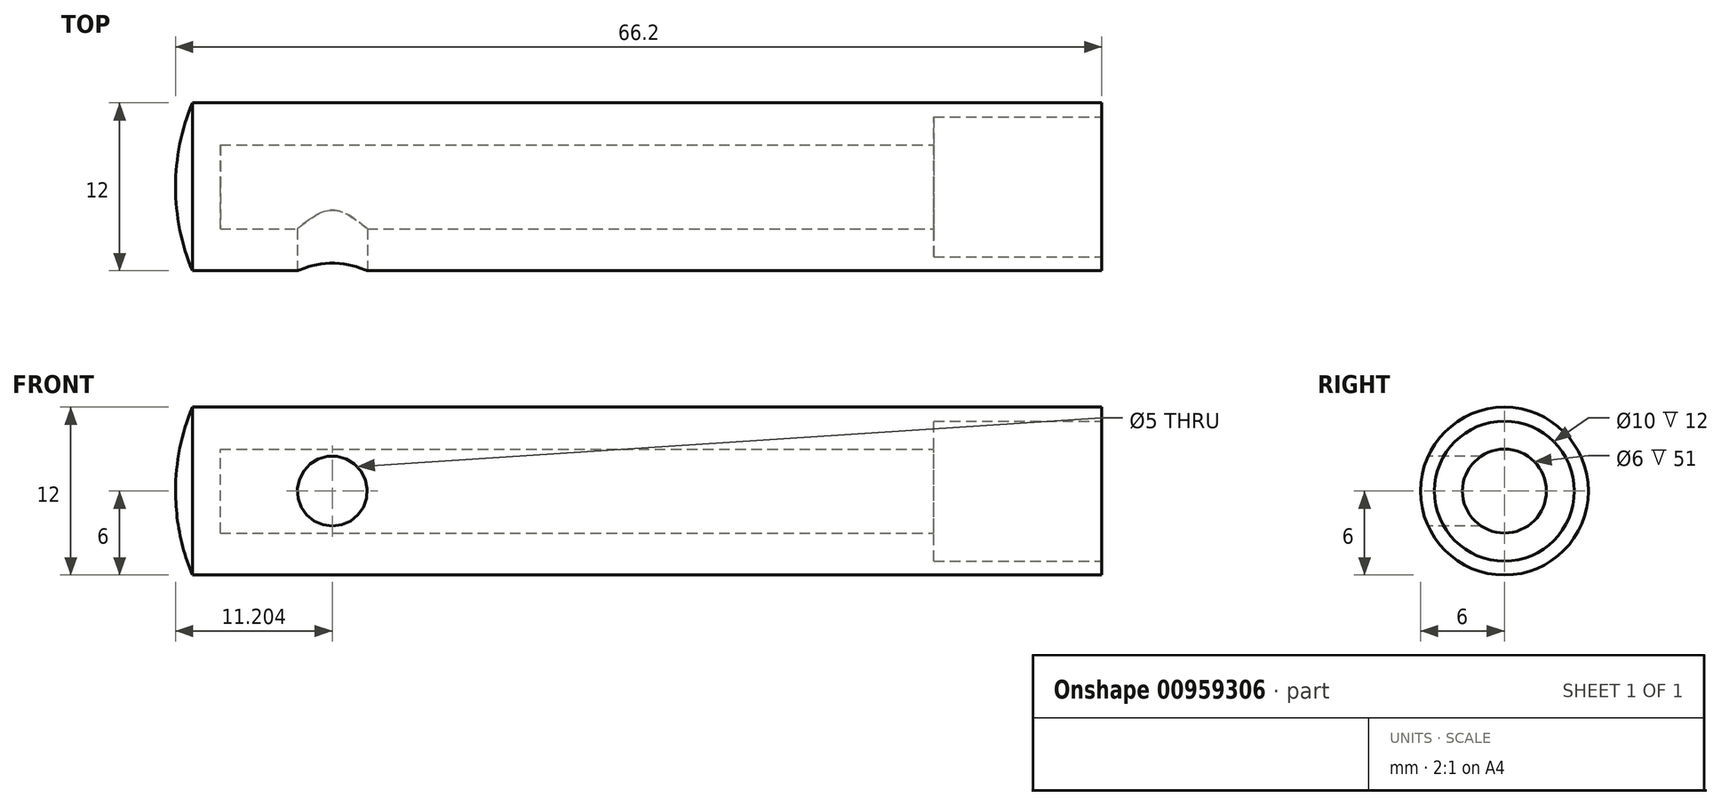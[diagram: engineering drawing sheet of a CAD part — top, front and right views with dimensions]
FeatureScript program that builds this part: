
annotation { "Feature Type Name" : "Feature", "Feature Type Description" : "" }
export const myFeature = defineFeature(function(context is Context, id is Id, definition is map)
    precondition{}
    {
        {
            var Q0;
            Q0=qCreatedBy(makeId("Front.planeOp"),FACE);
            var sketch = newSketch(context, id + "F0", { "sketchPlane" : qUnion([Q0])});
            skLineSegment(sketch, "E0", {"start": v(-36.24, -6) * mm, "end": v(28.76, -6) * mm});
            skArc(sketch, "E1", {"start": v(-36.24, -6) * mm, "mid": v(-37.14, -3.06) * mm, "end": v(-37.44, 0) * mm});
            skLineSegment(sketch, "E2", {"start": v(28.76, -6) * mm, "end": v(28.76, 0) * mm});
            skLineSegment(sketch, "E3", {"start": v(28.76, 0) * mm, "end": v(-37.44, 0) * mm});
            skSolve(sketch);
        }
        {
            var Q0;
            Q0=makeQuery(id+"F0.imprint","IMPRINT",FACE,{"disambiguationData":[TD([[makeQuery(id+"F0.imprint","IMPRINT",EDGE,{"derivedFrom":sQuery(id+"F0.wireOp",EDGE,"E0")}),1.0]])]});
            var Q1;
            Q1=sQuery(id+"F0.wireOp",EDGE,"E3");
            revolve(context, id + "F1", {"surfaceOperationType" : NewSurfaceOperationType.NEW, "entities" : qUnion([Q0]), "axis" : qUnion([Q1]), "revolveType" : RevolveType.FULL});
        }
        {
            var Q0;
            Q0=makeQuery(id+"F1.opRevolve","SWEPT_FACE",FACE,{"disambiguationData":[OSD([sQuery(id+"F0.wireOp",EDGE,"E2")])]});
            var sketch = newSketch(context, id + "F2", { "sketchPlane" : qUnion([Q0])});
            skCircle(sketch, "E4", {"center": v(0, 0) * mm, "radius": 3 * mm});
            skSolve(sketch);
        }
        {
            var Q0;
            Q0 = qSketchRegion(id + "F2", true);
            extrude(context, id + "F3", {"entities" : qUnion([Q0]), "operationType" : NewBodyOperationType.REMOVE, "oppositeDirection" : true, "depth" : 63 * mm, "offsetDistance" : 25.4 * mm});
        }
        {
            var Q0;
            Q0=makeQuery(id+"F1.opRevolve","SWEPT_FACE",FACE,{"disambiguationData":[OSD([sQuery(id+"F0.wireOp",EDGE,"E2")])]});
            var sketch = newSketch(context, id + "F4", { "sketchPlane" : qUnion([Q0])});
            skCircle(sketch, "E5", {"center": v(0, 0) * mm, "radius": 5 * mm});
            skSolve(sketch);
        }
        {
            var Q0;
            Q0 = qSketchRegion(id + "F4", true);
            extrude(context, id + "F5", {"entities" : qUnion([Q0]), "operationType" : NewBodyOperationType.REMOVE, "oppositeDirection" : true, "depth" : 12 * mm, "offsetDistance" : 25.4 * mm});
        }
        {
            var Q0;
            Q0=qCreatedBy(makeId("Top.planeOp"),FACE);
            var sketch = newSketch(context, id + "F6", { "sketchPlane" : qUnion([Q0])});
            skLineSegment(sketch, "E6", {"start": v(-26.24, -11.93) * mm, "end": v(-23.74, -11.93) * mm});
            skLineSegment(sketch, "E7", {"start": v(-23.74, -11.93) * mm, "end": v(-23.74, 0) * mm});
            skLineSegment(sketch, "E8", {"start": v(-23.74, 0) * mm, "end": v(-26.24, 0) * mm});
            skLineSegment(sketch, "E9", {"start": v(-26.24, 0) * mm, "end": v(-26.24, -11.93) * mm});
            skSolve(sketch);
        }
        {
            var Q0;
            Q0 = qSketchRegion(id + "F6", true);
            var Q1;
            Q1=sQuery(id+"F6.wireOp",EDGE,"E9");
            revolve(context, id + "F7", {"operationType" : NewBodyOperationType.REMOVE, "surfaceOperationType" : NewSurfaceOperationType.NEW, "entities" : qUnion([Q0]), "axis" : qUnion([Q1]), "revolveType" : RevolveType.FULL, "oppositeDirection" : true});
        }
    });
